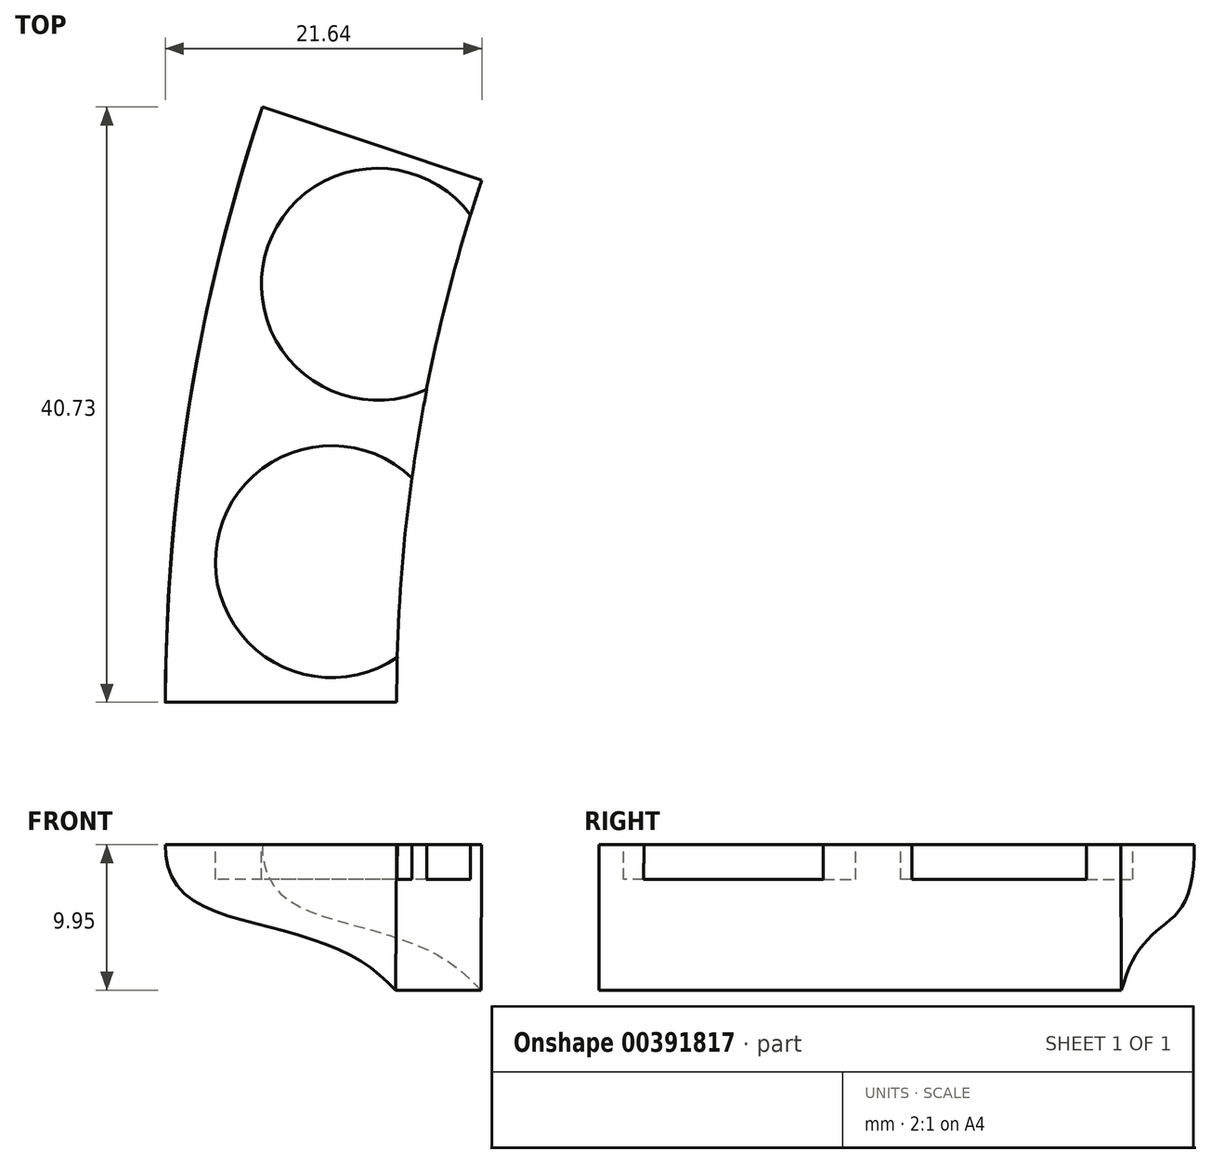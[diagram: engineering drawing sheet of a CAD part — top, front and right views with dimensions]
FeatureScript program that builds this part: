
annotation { "Feature Type Name" : "Feature", "Feature Type Description" : "" }
export const myFeature = defineFeature(function(context is Context, id is Id, definition is map)
    precondition{}
    {
        {
            var Q0;
            Q0=qCreatedBy(makeId("Front.planeOp"),FACE);
            var sketch = newSketch(context, id + "F0", { "sketchPlane" : qUnion([Q0])});
            skLineSegment(sketch, "E0", {"start": v(136.76, 20.95) * mm, "end": v(136.76, -4.3) * mm});
            skFitSpline(sketch, "E1", {"points": [v(27.23, 21.65) * mm, v(23.01, 21.51) * mm, v(16.87, 20.5) * mm, v(10.67, 17.87) * mm, v(8.42, 14) * mm, v(9.76, 10.6) * mm, v(14.88, 8.52) * mm, v(21.2, 6.37) * mm, v(24.6, 3.63) * mm, v(27.23, 1.02) * mm], "startDerivative": vector(-39.66, 0.87) * mm, "endDerivative": vector(16.8, -19) * mm});
            skLineSegment(sketch, "E2", {"start": v(24.23, 14) * mm, "end": v(24.17, 4.04) * mm});
            skPoint(sketch, "E3.start.orphan", {"position": v(39.93, 21.68) * mm});
            skLineSegment(sketch, "E4", {"start": v(136.76, 20.95) * mm, "end": v(39.93, 21.68) * mm});
            skLineSegment(sketch, "E5", {"start": v(136.76, 20.95) * mm, "end": v(19.42, 21.84) * mm});
            skLineSegment(sketch, "E6", {"start": v(8.42, 14) * mm, "end": v(24.23, 14) * mm});
            skPoint(sketch, "E7.orphan", {"position": v(24.28, 21.65) * mm});
            skSolve(sketch);
        }
        {
            var Q0;
            Q0 = qSketchRegion(id + "F0", true);
            var Q1;
            Q1=sQuery(id+"F0.wireOp",EDGE,"E0");
            revolve(context, id + "F1", {"entities" : qUnion([Q0]), "axis" : qUnion([Q1]), "revolveType" : RevolveType.ONE_DIRECTION, "angle" : 18.5 * degree});
        }
        {
            var Q0;
            Q0=makeQuery(id+"F1.opRevolve","SWEPT_FACE",FACE,{"disambiguationData":[OSD([sQuery(id+"F0.wireOp",EDGE,"E6")])]});
            var sketch = newSketch(context, id + "F2", { "sketchPlane" : qUnion([Q0])});
            skPoint(sketch, "E8.endSnap0", {"position": v(25.7, 18.09) * mm});
            skPoint(sketch, "E9.orphan", {"position": v(23.3, 28.5) * mm});
            skPoint(sketch, "E10.orphan", {"position": v(20.16, 9.59) * mm});
            skCircle(sketch, "E11", {"center": v(22.91, 28.6) * mm, "radius": 7.94 * mm});
            skCircle(sketch, "E12", {"center": v(19.77, 9.62) * mm, "radius": 7.94 * mm});
            skSolve(sketch);
        }
        {
            var Q0;
            Q0 = qSketchRegion(id + "F2", true);
            extrude(context, id + "F3", {"entities" : qUnion([Q0]), "operationType" : NewBodyOperationType.REMOVE, "oppositeDirection" : true, "depth" : 2.38 * mm});
        }
    });
